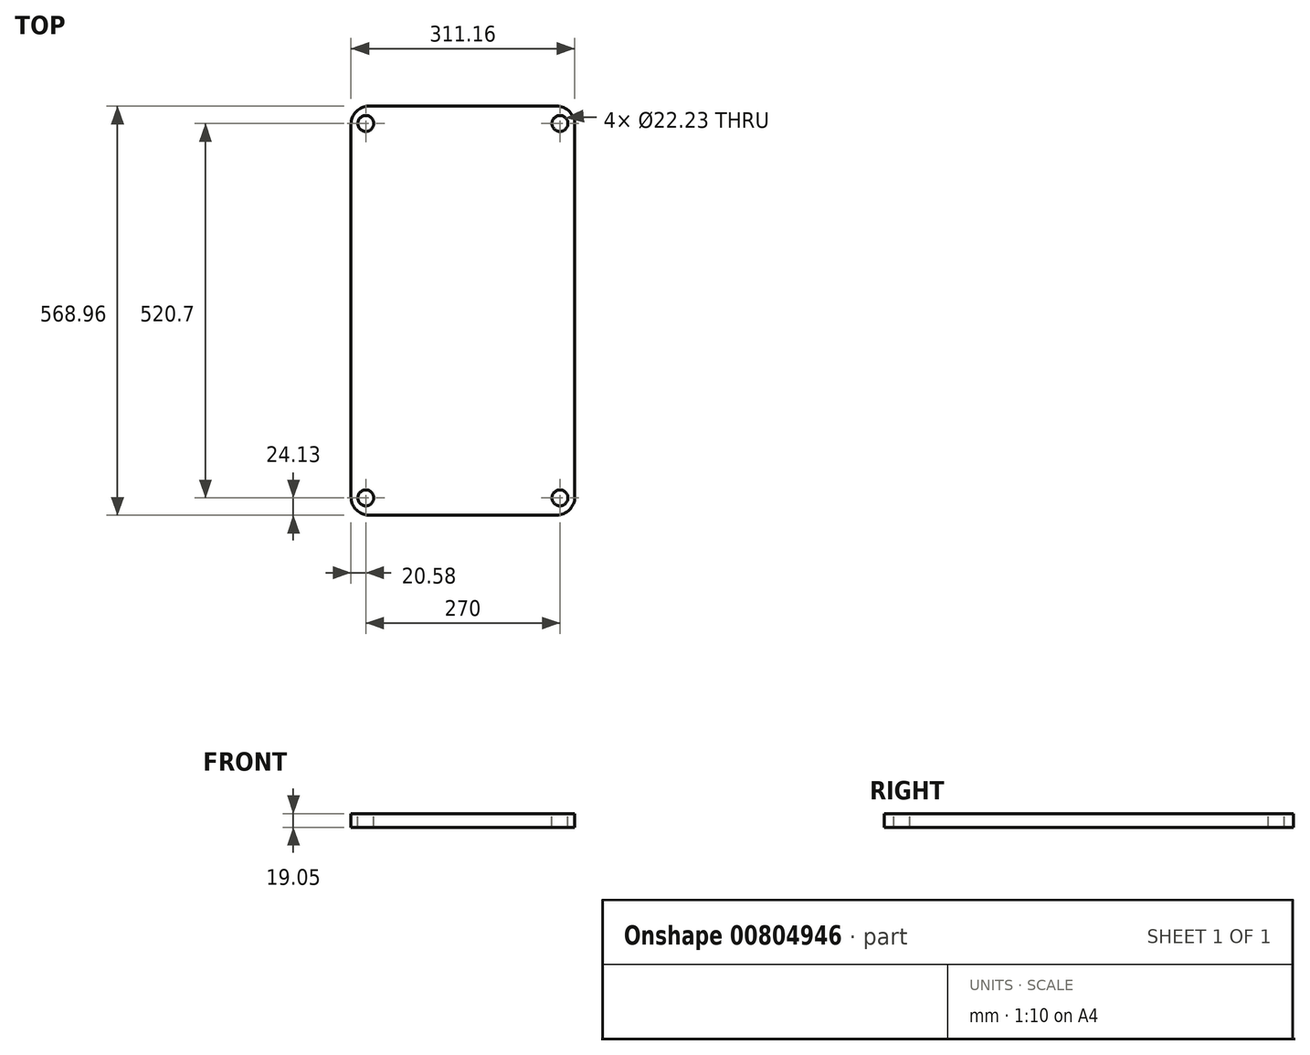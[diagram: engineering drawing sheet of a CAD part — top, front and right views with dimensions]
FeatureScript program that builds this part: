
annotation { "Feature Type Name" : "Feature", "Feature Type Description" : "" }
export const myFeature = defineFeature(function(context is Context, id is Id, definition is map)
    precondition{}
    {
        {
            var Q0;
            Q0=qCreatedBy(makeId("Top.planeOp"),FACE);
            var sketch = newSketch(context, id + "F0", { "sketchPlane" : qUnion([Q0])});
            skLineSegment(sketch, "E0.bottom", {"start": v(-155.57, 284.48) * mm, "end": v(155.58, 284.48) * mm});
            skLineSegment(sketch, "E0.top", {"start": v(-155.58, -284.48) * mm, "end": v(155.57, -284.48) * mm});
            skLineSegment(sketch, "E0.left", {"start": v(-155.57, 284.48) * mm, "end": v(-155.58, -284.48) * mm});
            skLineSegment(sketch, "E0.right", {"start": v(155.58, 284.48) * mm, "end": v(155.57, -284.48) * mm});
            skPoint(sketch, "E0.middle", {"position": v(0, 0) * mm});
            skSolve(sketch);
        }
        {
            var Q0;
            Q0 = qSketchRegion(id + "F0", true);
            extrude(context, id + "F1", {"entities" : qUnion([Q0]), "depth" : 19.05 * mm, "offsetDistance" : 25.4 * mm});
        }
        {
            var Q0;
            Q0=makeQuery(id+"F1.opExtrude","CAP_FACE",FACE,{"disambiguationData":[OSD([sQuery(id+"F0.wireOp",EDGE,"E0.bottom"),sQuery(id+"F0.wireOp",EDGE,"E0.top"),sQuery(id+"F0.wireOp",EDGE,"E0.left"),sQuery(id+"F0.wireOp",EDGE,"E0.right")])],"isStart":false});
            var sketch = newSketch(context, id + "F2", { "sketchPlane" : qUnion([Q0])});
            skLineSegment(sketch, "E1.bottom", {"start": v(135, -260.35) * mm, "end": v(-135, -260.35) * mm, "construction": true});
            skLineSegment(sketch, "E1.top", {"start": v(135, 260.35) * mm, "end": v(-135, 260.35) * mm, "construction": true});
            skLineSegment(sketch, "E1.left", {"start": v(135, -260.35) * mm, "end": v(135, 260.35) * mm, "construction": true});
            skLineSegment(sketch, "E1.right", {"start": v(-135, -260.35) * mm, "end": v(-135, 260.35) * mm, "construction": true});
            skPoint(sketch, "E1.middle", {"position": v(0, 0) * mm});
            skCircle(sketch, "E2", {"center": v(-135, 260.35) * mm, "radius": 11.11 * mm});
            skCircle(sketch, "E3", {"center": v(135, 260.35) * mm, "radius": 11.11 * mm});
            skCircle(sketch, "E4", {"center": v(135, -260.35) * mm, "radius": 11.11 * mm});
            skCircle(sketch, "E5", {"center": v(-135, -260.35) * mm, "radius": 11.11 * mm});
            skSolve(sketch);
        }
        {
            var Q0;
            Q0=makeQuery(id+"F1.opExtrude","SWEPT_EDGE",EDGE,{"disambiguationData":[OSD([sQuery(id+"F0.wireOp",EDGE,"E0.top"),sQuery(id+"F0.wireOp",EDGE,"E0.right")])]});
            var Q1;
            Q1=makeQuery(id+"F1.opExtrude","SWEPT_EDGE",EDGE,{"disambiguationData":[OSD([sQuery(id+"F0.wireOp",EDGE,"E0.top"),sQuery(id+"F0.wireOp",EDGE,"E0.left")])]});
            var Q2;
            Q2=makeQuery(id+"F1.opExtrude","SWEPT_EDGE",EDGE,{"disambiguationData":[OSD([sQuery(id+"F0.wireOp",EDGE,"E0.bottom"),sQuery(id+"F0.wireOp",EDGE,"E0.left")])]});
            var Q3;
            Q3=makeQuery(id+"F1.opExtrude","SWEPT_EDGE",EDGE,{"disambiguationData":[OSD([sQuery(id+"F0.wireOp",EDGE,"E0.bottom"),sQuery(id+"F0.wireOp",EDGE,"E0.right")])]});
            fillet(context, id + "F3", {"entities" : qUnion([Q0, Q1, Q2, Q3]), "radius" : 25.4 * mm, "tangentPropagation" : true, "allowEdgeOverflow" : false});
        }
        {
            var Q0;
            Q0 = qSketchRegion(id + "F2", true);
            extrude(context, id + "F4", {"entities" : qUnion([Q0]), "operationType" : NewBodyOperationType.REMOVE, "endBound" : BoundingType.THROUGH_ALL, "oppositeDirection" : true, "depth" : 25.4 * mm, "offsetDistance" : 25.4 * mm});
        }
    });
